# Revit family: Hager-Volta-IP30-Hollow_wall-syst-SE-en
name_source: partatom
category: Electrical Equipment
units: mm (PartAtom-declared; Revit-internal decimal feet)

## family parameters
Cut with Voids When Loaded = No
Host = Face
Panel Configuration = Two Columns, Circuits Across
Part Type = Panelboard
Room Calculation Point = No
Round Connector Dimension = Use Diameter
Shared = No

## types (7) — shared parameters
EF000003 - Mounting method = EV000128 - Hollow wall
EF000007 - Colour = EV000202 - White
EF000008 - Width = 348 mm  [stored 1.14173 ft]
EF000049 - Depth = 94 mm  [stored 0.308399 ft]
EF000116 - RAL-number = 9010
EF000218 - Built-in depth = 90 mm  [stored 0.295276 ft]
EF000339 - Type of cover = EV004216 - Door
EF000846 - Built-in width = 314 mm  [stored 1.03018 ft]
EF001062 - EMC-version = No
EF001088 - Extension possible = Yes
EF001131 - Internal depth = 92 mm
EF001134 - DIN-rail = Yes
EF002950 - Width in number of modular spacings = 12
EF004462 - Type of closure = EV000154 - Other
EF005474 - Degree of protection (IP) = EV006410 - IP30
EF006244 - Transparent cover/door = No
EF006306 - With lock = No
EF009212 - Cover model = EV009916 - With notch
EF015776 - Earthing terminal block = Yes
EF015941 - Signal passing door = No
HG000001 - Number of columns = 1
HG000002 - With door or cover = Yes
HG000003 - Range = Volta
HG000005 - Thickness = 3 mm  [stored 0.00984252 ft]
HG000006 - Flush mounted = Yes
HG000009 - Double swing door = No
HG000010 - Asymmetric doors = No
HG000011 - Empty rows from bottom = No
HG000017 - Distance between poles = 18 mm  [stored 0.0590551 ft]
Manufacturer = Hager
Type Comments = Volta
zero-valued in all types: Default Elevation, HG000007 - Number of empty columns, HG000008 - Number of empty rows

## per-type parameters (varying)
| type | EF000040 - Height | EF000118 - With mounting plate | EF000266 - Number of rows | EF000332 - Built-in height | EF001596 - Material housing | EF015777 - Neutral terminal block | HG000004 - Manufacturer reference | Model |
| Recessed mounted IP30 W348 H356.5 D94.5 12 Modular spacings - VH12NN | 356 mm | No | 1 | 321 mm | EV000139 - Plastic | Yes | VH12NN | VH12NN |
| Recessed mounted IP30 W348 H505.5 D94.5 12 Modular spacings - VH24NN | 506 mm | No | 2 | 470 mm | EV000139 - Plastic | Yes | VH24NN | VH24NN |
| Recessed mounted IP30 W348 H630.5 D94.5 12 Modular spacings - VH36NMB | 630 mm | Yes | 3 | 595 mm | EV000154 - Other | No | VH36NMB | VH36NMB |
| Recessed mounted IP30 W348 H630.5 D94.5 12 Modular spacings - VH36NN | 630 mm | No | 3 | 595 mm | EV000139 - Plastic | Yes | VH36NN | VH36NN |
| Recessed mounted IP30 W348 H755.5 D94.5 12 Modular spacings - VH48NMB | 756 mm | Yes | 4 | 720 mm  [stored 2.3622 ft] | EV000154 - Other | No | VH48NMB | VH48NMB |
| Recessed mounted IP30 W348 H755.5 D94.5 12 Modular spacings - VH48NN | 756 mm | No | 4 | 720 mm  [stored 2.3622 ft] | EV000139 - Plastic | Yes | VH48NN | VH48NN |
| Recessed mounted IP30 W348 H880.5 D94.5 12 Modular spacings - VH60NN | 880 mm  [stored 2.88714 ft] | Yes | 5 | 880 mm  [stored 2.88714 ft] | EV000154 - Other | No | VH60NN | VH60NN |

note: [stored X ft] marks values corroborated as IEEE doubles in the binary element streams (Revit-internal decimal feet)

## geometry (parser evidence)
native form markers: Sweep x17
no freeform markers — native parametric forms only
